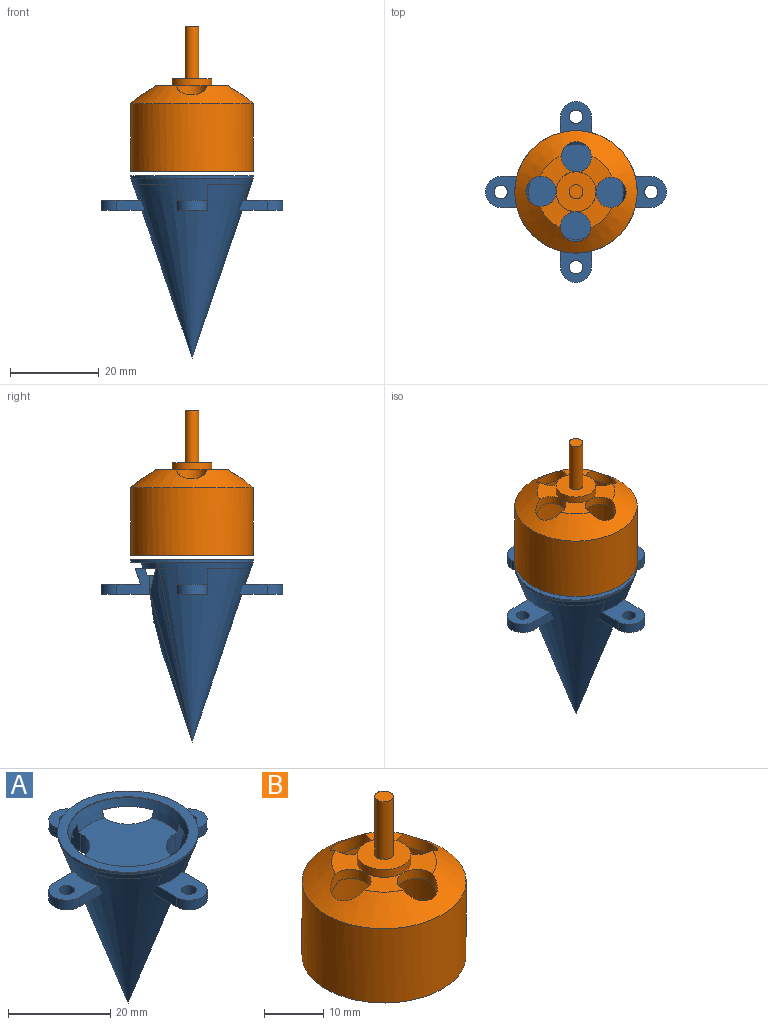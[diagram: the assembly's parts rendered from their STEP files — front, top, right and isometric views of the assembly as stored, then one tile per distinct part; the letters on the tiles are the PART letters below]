
ASSEMBLY  parts=2 mates=1
PART A: 36 faces, bbox 40.9x40.9x7.8 mm
  f0: cone r=12.1mm half-angle=18.8deg, axis (0,0,1), area 0.7mm2, adj f1,f2,f3,f4
  f1: cylinder r=13.8mm len=27.6mm, axis (0,0,1), area 43.4mm2, adj f0,f5
  f2: cone r=12.1mm half-angle=18.8deg, axis (0,0,1), area 196.3mm2, adj f0,f3,f6,f7,f8,f9,f10,f11
  f3: plane 8.87x7mm, normal (0,0,1), area 47.3mm2, adj f0,f2,f4,f8,f20,f21
  f4: plane 7.31x5.92mm, normal (0,1,0), area 24.9mm2, adj f0,f3,f7,f21,f22,f23,f24,f25
  f5: plane 27.6x27.6mm, normal (0,0,1), area 160.8mm2, adj f1,f26
  f6: plane 7.31x5.92mm, normal (1,0,0), area 24.9mm2, adj f2,f7,f19,f22,f23,f24,f25,f27
  f7: plane 9.36x9.36mm, normal (0,0,-1), area 25.7mm2, adj f2,f4,f6,f25
  f8: plane 7.31x5.92mm, normal (0,-1,0), area 24.9mm2, adj f2,f3,f9,f21,f22,f24,f25,f28
  f9: plane 9.36x9.36mm, normal (0,0,-1), area 25.7mm2, adj f2,f8,f10,f25
  f10: plane 7.31x5.92mm, normal (1,0,0), area 24.9mm2, adj f2,f9,f11,f22,f24,f25,f28,f29
  f11: plane 8.87x7mm, normal (0,0,1), area 47.3mm2, adj f2,f10,f12,f29,f30
  f12: plane 7.31x5.92mm, normal (-1,0,0), area 24.9mm2, adj f2,f11,f13,f22,f24,f25,f29,f31
  f13: plane 9.36x9.36mm, normal (0,0,-1), area 25.7mm2, adj f2,f12,f14,f25
  f14: plane 7.31x5.92mm, normal (0,-1,0), area 24.9mm2, adj f2,f13,f15,f22,f24,f25,f31,f32
  f15: plane 8.87x7mm, normal (0,0,1), area 47.3mm2, adj f2,f14,f16,f32,f33
  f16: plane 7.31x5.92mm, normal (0,1,0), area 24.9mm2, adj f2,f15,f17,f22,f24,f25,f32,f34
  f17: plane 9.36x9.36mm, normal (0,0,-1), area 25.7mm2, adj f2,f16,f18,f25
  f18: plane 7.31x5.92mm, normal (-1,0,0), area 24.9mm2, adj f2,f17,f19,f22,f24,f25,f27,f34
  f19: plane 8.87x7mm, normal (0,0,1), area 47.3mm2, adj f2,f6,f18,f27,f35
  f20: cylinder r=1.5mm len=3mm, axis (0,0,1), area 21.7mm2, adj f3,f22
  f21: cylinder r=3.5mm len=7mm, axis (0,0,1), area 25.3mm2, adj f3,f4,f8,f22
  f22: plane 40.9x40.9mm, normal (0,0,-1), area 506.8mm2, adj f4,f6,f8,f10,f12,f14,f16,f18
  f23: cylinder r=6.16mm len=6.16mm, axis (0,0,-1), area 41.6mm2, adj f4,f6,f22,f24
  f24: plane 21.34x21.34mm, normal (0,0,1), area 276.8mm2, adj f4,f6,f8,f10,f12,f14,f16,f18
  f25: cone r=10.21mm half-angle=18.8deg, axis (0,0,1), area 180.3mm2, adj f4,f6,f7,f8,f9,f10,f12,f13
  f26: cylinder r=11.8mm len=23.6mm, axis (0,0,1), area 12.6mm2, adj f5,f25
  f27: cylinder r=3.5mm len=7mm, axis (0,0,1), area 25.3mm2, adj f6,f18,f19,f22
  f28: cylinder r=6.16mm len=6.16mm, axis (0,0,-1), area 41.6mm2, adj f8,f10,f22,f24
  f29: cylinder r=3.5mm len=7mm, axis (0,0,1), area 25.3mm2, adj f10,f11,f12,f22
  f30: cylinder r=1.5mm len=3mm, axis (0,0,1), area 21.7mm2, adj f11,f22
  f31: cylinder r=6.16mm len=6.16mm, axis (0,0,-1), area 41.6mm2, adj f12,f14,f22,f24
  f32: cylinder r=3.5mm len=7mm, axis (0,0,1), area 25.3mm2, adj f14,f15,f16,f22
  f33: cylinder r=1.5mm len=3mm, axis (0,0,1), area 21.7mm2, adj f15,f22
  f34: cylinder r=6.16mm len=6.16mm, axis (0,0,-1), area 41.6mm2, adj f16,f18,f22,f24
  f35: cylinder r=1.5mm len=3mm, axis (0,0,1), area 21.7mm2, adj f19,f22
PART B: 20 faces, bbox 27.6x27.6x32.8 mm
  f0: plane 8.12x8.12mm, normal (0,0,1), area 22.2mm2, adj f6,f7,f18,f19
  f1: plane 8.12x8.12mm, normal (0,0,1), area 22.2mm2, adj f6,f7,f17,f18
  f2: plane 8.12x8.12mm, normal (0,0,1), area 22.2mm2, adj f6,f7,f16,f17
  f3: cylinder r=13.8mm len=27.6mm, axis (0,0,1), area 1326.6mm2, adj f4,f6
  f4: plane 27.6x27.6mm, normal (0,0,-1), area 153.4mm2, adj f3,f11
  f5: plane 8.12x8.12mm, normal (0,0,1), area 22.2mm2, adj f6,f7,f16,f19
  f6: cone r=8.8mm half-angle=51.3deg, axis (0,0,-1), area 385.2mm2, adj f0,f1,f2,f3,f5,f16,f17,f18
  f7: cylinder r=4.5mm len=9mm, axis (0,0,-1), area 45.2mm2, adj f0,f1,f2,f5,f8
  f8: plane 9x9mm, normal (0,0,1), area 55.9mm2, adj f7,f9
  f9: cylinder r=1.57mm len=11.9mm, axis (0,0,-1), area 117.4mm2, adj f8,f10
  f10: plane 3.14x3.14mm, normal (0,0,1), area 7.7mm2, adj f9
  f11: cylinder r=11.9mm len=23.8mm, axis (0,0,1), area 1075.7mm2, adj f4,f13
  f12: plane 14.81x14.81mm, normal (0,0,-1), area 114.2mm2, adj f13,f14,f16,f17,f18,f19
  f13: cone r=7.61mm half-angle=51.3deg, axis (0,0,-1), area 210.3mm2, adj f11,f12,f16,f17,f18,f19
  f14: cylinder r=2.6mm len=5.2mm, axis (0,0,-1), area 26.1mm2, adj f12,f15
  f15: plane 5.2x5.2mm, normal (0,0,-1), area 21.2mm2, adj f14
  f16: cylinder r=3.4mm len=6.8mm, axis (0,0,1), area 46.4mm2, adj f2,f5,f6,f12,f13
  f17: cylinder r=3.4mm len=6.8mm, axis (0,0,1), area 46.4mm2, adj f1,f2,f6,f12,f13
  f18: cylinder r=3.4mm len=6.8mm, axis (0,0,1), area 46.4mm2, adj f0,f1,f6,f12,f13
  f19: cylinder r=3.4mm len=6.8mm, axis (0,0,1), area 46.4mm2, adj f0,f5,f6,f12,f13
PLACE A t=(1.38,-3.22,35.13)mm fixed
PLACE B rot(axis=(0,0,-1),0.8deg) t=(1.38,-3.22,35.73)mm
MATE revolute B.f3 <-> A.f0  axis (0,0,1) through (1.38,-3.22,16.43)mm
